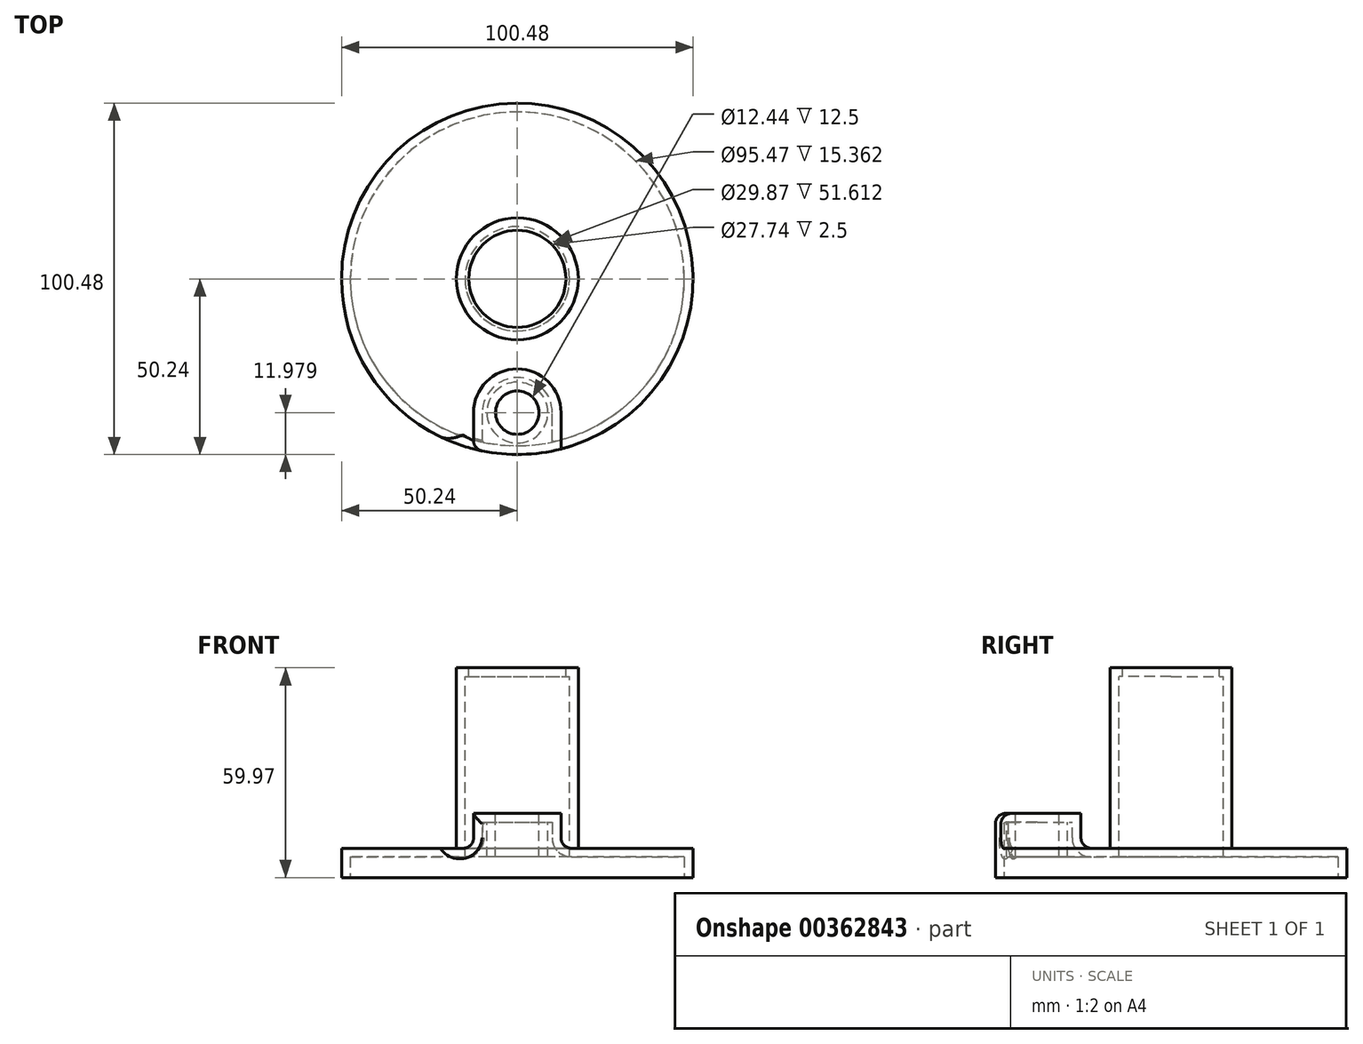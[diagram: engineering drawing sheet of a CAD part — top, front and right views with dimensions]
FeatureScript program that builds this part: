
annotation { "Feature Type Name" : "Feature", "Feature Type Description" : "" }
export const myFeature = defineFeature(function(context is Context, id is Id, definition is map)
    precondition{}
    {
        {
            var Q0;
            Q0=qCreatedBy(makeId("Right.planeOp"),FACE);
            var sketch = newSketch(context, id + "F0", { "sketchPlane" : qUnion([Q0])});
            skLineSegment(sketch, "E0.bottom", {"start": v(0, 0) * mm, "end": v(-50.24, 0) * mm});
            skLineSegment(sketch, "E0.top", {"start": v(0, 59.97) * mm, "end": v(-50.24, 59.97) * mm});
            skLineSegment(sketch, "E0.left", {"start": v(0, 0) * mm, "end": v(0, 59.97) * mm});
            skLineSegment(sketch, "E0.right", {"start": v(-50.24, 0) * mm, "end": v(-50.24, 59.97) * mm});
            skLineSegment(sketch, "E1", {"start": v(0, -25.53) * mm, "end": v(0, 77.83) * mm, "construction": true});
            skSolve(sketch);
        }
        {
            var Q0;
            Q0 = qSketchRegion(id + "F0", true);
            var Q1;
            Q1=sQuery(id+"F0.wireOp",EDGE,"E1");
            revolve(context, id + "F1", {"entities" : qUnion([Q0]), "axis" : qUnion([Q1]), "revolveType" : RevolveType.FULL});
        }
        {
            var Q0;
            Q0=qCreatedBy(makeId("Right.planeOp"),FACE);
            var sketch = newSketch(context, id + "F2", { "sketchPlane" : qUnion([Q0])});
            skLineSegment(sketch, "E2.bottom", {"start": v(-70.29, 84.7) * mm, "end": v(-17.44, 84.7) * mm});
            skLineSegment(sketch, "E2.top", {"start": v(-70.29, 18.36) * mm, "end": v(-17.44, 18.36) * mm});
            skLineSegment(sketch, "E2.left", {"start": v(-70.29, 84.7) * mm, "end": v(-70.29, 18.36) * mm});
            skLineSegment(sketch, "E2.right", {"start": v(-17.44, 84.7) * mm, "end": v(-17.44, 18.36) * mm});
            skSolve(sketch);
        }
        {
            var Q0;
            Q0=makeQuery(id+"F2.imprint","IMPRINT",FACE,{"disambiguationData":[TD([[makeQuery(id+"F2.imprint","IMPRINT",EDGE,{"derivedFrom":sQuery(id+"F2.wireOp",EDGE,"E2.bottom")}),-1.0]])]});
            var Q1;
            Q1=sQuery(id+"F0.wireOp",EDGE,"E1");
            revolve(context, id + "F3", {"operationType" : NewBodyOperationType.REMOVE, "entities" : qUnion([Q0]), "axis" : qUnion([Q1]), "revolveType" : RevolveType.FULL, "oppositeDirection" : true});
        }
        {
            var Q0;
            Q0=makeQuery(id+"F3.boolean.opBoolean","COPY",FACE,{"derivedFrom":makeQuery(id+"F3.opRevolve","SWEPT_FACE",FACE,{"disambiguationData":[OSD([sQuery(id+"F2.wireOp",EDGE,"E2.top")])]})});
            var sketch = newSketch(context, id + "F4", { "sketchPlane" : qUnion([Q0])});
            skLineSegment(sketch, "E3", {"start": v(0, -68.26) * mm, "end": v(0, -38.26) * mm});
            skArc(sketch, "E4.0.startCap", {"start": v(12.5, -68.26) * mm, "mid": v(0, -80.76) * mm, "end": v(-12.5, -68.26) * mm});
            skArc(sketch, "E4.0.endCap", {"start": v(-12.5, -38.26) * mm, "mid": v(0, -25.76) * mm, "end": v(12.5, -38.26) * mm});
            skLineSegment(sketch, "E4.0.left", {"start": v(-12.5, -68.26) * mm, "end": v(-12.5, -38.26) * mm});
            skLineSegment(sketch, "E4.0.right", {"start": v(12.5, -68.26) * mm, "end": v(12.5, -38.26) * mm});
            skCircle(sketch, "E5", {"center": v(0, -38.26) * mm, "radius": 6.22 * mm});
            skSolve(sketch);
        }
        {
            var Q0;
            {var subQ1=sQuery(id+"F4.wireOp",EDGE,"E4.0.endCap");Q0=makeQuery(id+"F4.imprint","IMPRINT",FACE,{"disambiguationData":[TD([[makeQuery(id+"F4.imprint","IMPRINT",EDGE,{"derivedFrom":subQ1}),-1.0]])]});}
            var Q1;
            Q1=makeQuery(id+"F4.imprint","IMPRINT",FACE,{"disambiguationData":[TD([[makeQuery(id+"F4.imprint","IMPRINT",EDGE,{"derivedFrom":sQuery(id+"F4.wireOp",EDGE,"E5")}),1.0]])]});
            extrude(context, id + "F5", {"entities" : qUnion([Q0, Q1]), "operationType" : NewBodyOperationType.REMOVE, "oppositeDirection" : true, "depth" : 10 * mm});
        }
        {
            var Q0;
            Q0=makeQuery(id+"Ff13ZRt0uXcgMN7_1.3.F5.boolean.opBoolean","COPY",EDGE,{"derivedFrom":makeQuery(id+"Ff13ZRt0uXcgMN7_1.3.F5.opExtrude","CAP_EDGE",EDGE,{"disambiguationData":[OSD([sQuery(id+"F4.wireOp",EDGE,"E4.0.left")])],"isStart":true})});
            var Q1;
            Q1=makeQuery(id+"Ff13ZRt0uXcgMN7_1.4.F5.boolean.opBoolean","COPY",EDGE,{"derivedFrom":makeQuery(id+"Ff13ZRt0uXcgMN7_1.4.F5.opExtrude","CAP_EDGE",EDGE,{"disambiguationData":[OSD([sQuery(id+"F4.wireOp",EDGE,"E4.0.right")])],"isStart":true})});
            var Q2;
            Q2=makeQuery(id+"Ff13ZRt0uXcgMN7_1.2.F5.boolean.opBoolean","COPY",EDGE,{"derivedFrom":makeQuery(id+"Ff13ZRt0uXcgMN7_1.2.F5.opExtrude","CAP_EDGE",EDGE,{"disambiguationData":[OSD([sQuery(id+"F4.wireOp",EDGE,"E4.0.left")])],"isStart":true})});
            var Q3;
            Q3=makeQuery(id+"Ff13ZRt0uXcgMN7_1.1.F5.boolean.opBoolean","COPY",EDGE,{"derivedFrom":makeQuery(id+"Ff13ZRt0uXcgMN7_1.1.F5.opExtrude","CAP_EDGE",EDGE,{"disambiguationData":[OSD([sQuery(id+"F4.wireOp",EDGE,"E4.0.left")])],"isStart":true})});
            var Q4;
            Q4=makeQuery(id+"F5.boolean.opBoolean","COPY",EDGE,{"derivedFrom":makeQuery(id+"F5.opExtrude","CAP_EDGE",EDGE,{"disambiguationData":[OSD([sQuery(id+"F4.wireOp",EDGE,"E4.0.left")])],"isStart":true})});
            var Q5;
            Q5=makeQuery(id+"Ff13ZRt0uXcgMN7_1.1.F5.boolean.opBoolean","COPY",EDGE,{"derivedFrom":makeQuery(id+"Ff13ZRt0uXcgMN7_1.1.F5.opExtrude","CAP_EDGE",EDGE,{"disambiguationData":[OSD([sQuery(id+"F4.wireOp",EDGE,"E4.0.endCap")])],"isStart":false})});
            var Q6;
            Q6=makeQuery(id+"Ff13ZRt0uXcgMN7_1.2.F5.boolean.opBoolean","COPY",EDGE,{"derivedFrom":makeQuery(id+"Ff13ZRt0uXcgMN7_1.2.F5.opExtrude","CAP_EDGE",EDGE,{"disambiguationData":[OSD([sQuery(id+"F4.wireOp",EDGE,"E4.0.endCap")])],"isStart":false})});
            var Q7;
            Q7=makeQuery(id+"Ff13ZRt0uXcgMN7_1.3.F5.boolean.opBoolean","COPY",EDGE,{"derivedFrom":makeQuery(id+"Ff13ZRt0uXcgMN7_1.3.F5.opExtrude","CAP_EDGE",EDGE,{"disambiguationData":[OSD([sQuery(id+"F4.wireOp",EDGE,"E4.0.left")])],"isStart":false})});
            var Q8;
            Q8=makeQuery(id+"Ff13ZRt0uXcgMN7_1.4.F5.boolean.opBoolean","COPY",EDGE,{"derivedFrom":makeQuery(id+"Ff13ZRt0uXcgMN7_1.4.F5.opExtrude","CAP_EDGE",EDGE,{"disambiguationData":[OSD([sQuery(id+"F4.wireOp",EDGE,"E4.0.right")])],"isStart":false})});
            var Q9;
            Q9=makeQuery(id+"F5.boolean.opBoolean","COPY",EDGE,{"derivedFrom":makeQuery(id+"F5.opExtrude","CAP_EDGE",EDGE,{"disambiguationData":[OSD([sQuery(id+"F4.wireOp",EDGE,"E4.0.right")])],"isStart":false})});
            var Q10;
            {var subQ0=makeQuery(id+"F1.opRevolve","SWEPT_FACE",FACE,{"disambiguationData":[OSD([sQuery(id+"F0.wireOp",EDGE,"E0.right")])]});var subQ1=makeQuery(id+"Ff13ZRt0uXcgMN7_1.1.F5.opExtrude","SWEPT_FACE",FACE,{"disambiguationData":[OSD([sQuery(id+"F4.wireOp",EDGE,"E4.0.left")])]});var subQ2=makeQuery(id+"F3.opRevolve","SWEPT_FACE",FACE,{"disambiguationData":[OSD([sQuery(id+"F2.wireOp",EDGE,"E2.top")])]});var subQ4=sQuery(id+"F4.wireOp",EDGE,"E4.0.right");Q10=makeQuery(id+"Ff13ZRt0uXcgMN7_1.2.F5.boolean.opBoolean","SPLIT",EDGE,{"disambiguationData":[TD([makeQuery(id+"Ff13ZRt0uXcgMN7_1.1.F5.boolean.opBoolean","COPY",FACE,{"derivedFrom":subQ1})])],"derivedFrom":makeQuery(id+"Ff13ZRt0uXcgMN7_1.1.F5.boolean.opBoolean","SPLIT",EDGE,{"disambiguationData":[TD([makeQuery(id+"F5.boolean.opBoolean","COPY",FACE,{"derivedFrom":makeQuery(id+"F5.opExtrude","SWEPT_FACE",FACE,{"disambiguationData":[OSD([subQ4])]})})])],"derivedFrom":makeQuery(id+"F3.boolean.opBoolean","INTERSECT",EDGE,{"derivedFrom":[subQ0,subQ2]})})});}
            var Q11;
            {var subQ0=makeQuery(id+"F1.opRevolve","SWEPT_FACE",FACE,{"disambiguationData":[OSD([sQuery(id+"F0.wireOp",EDGE,"E0.right")])]});var subQ1=makeQuery(id+"F3.opRevolve","SWEPT_FACE",FACE,{"disambiguationData":[OSD([sQuery(id+"F2.wireOp",EDGE,"E2.top")])]});Q11=makeQuery(id+"Ff13ZRt0uXcgMN7_1.1.F5.boolean.opBoolean","SPLIT",EDGE,{"disambiguationData":[TD([makeQuery(id+"F5.boolean.opBoolean","COPY",FACE,{"derivedFrom":makeQuery(id+"F5.opExtrude","SWEPT_FACE",FACE,{"disambiguationData":[OSD([sQuery(id+"F4.wireOp",EDGE,"E4.0.left")])]})})])],"derivedFrom":makeQuery(id+"F3.boolean.opBoolean","INTERSECT",EDGE,{"derivedFrom":[subQ0,subQ1]})});}
            var Q12;
            {var subQ0=makeQuery(id+"F1.opRevolve","SWEPT_FACE",FACE,{"disambiguationData":[OSD([sQuery(id+"F0.wireOp",EDGE,"E0.right")])]});var subQ1=makeQuery(id+"F3.opRevolve","SWEPT_FACE",FACE,{"disambiguationData":[OSD([sQuery(id+"F2.wireOp",EDGE,"E2.top")])]});var subQ4=makeQuery(id+"F5.boolean.opBoolean","COPY",FACE,{"derivedFrom":makeQuery(id+"F5.opExtrude","SWEPT_FACE",FACE,{"disambiguationData":[OSD([sQuery(id+"F4.wireOp",EDGE,"E4.0.right")])]})});Q12=makeQuery(id+"Ff13ZRt0uXcgMN7_1.4.F5.boolean.opBoolean","SPLIT",EDGE,{"disambiguationData":[TD([subQ4])],"derivedFrom":makeQuery(id+"Ff13ZRt0uXcgMN7_1.3.F5.boolean.opBoolean","SPLIT",EDGE,{"disambiguationData":[TD([subQ4])],"derivedFrom":makeQuery(id+"Ff13ZRt0uXcgMN7_1.2.F5.boolean.opBoolean","SPLIT",EDGE,{"disambiguationData":[TD([subQ4])],"derivedFrom":makeQuery(id+"Ff13ZRt0uXcgMN7_1.1.F5.boolean.opBoolean","SPLIT",EDGE,{"disambiguationData":[TD([subQ4])],"derivedFrom":makeQuery(id+"F3.boolean.opBoolean","INTERSECT",EDGE,{"derivedFrom":[subQ0,subQ1]})})})})});}
            var Q13;
            {var subQ0=makeQuery(id+"F1.opRevolve","SWEPT_FACE",FACE,{"disambiguationData":[OSD([sQuery(id+"F0.wireOp",EDGE,"E0.right")])]});var subQ1=makeQuery(id+"F3.opRevolve","SWEPT_FACE",FACE,{"disambiguationData":[OSD([sQuery(id+"F2.wireOp",EDGE,"E2.top")])]});var subQ3=sQuery(id+"F4.wireOp",EDGE,"E4.0.left");var subQ4=makeQuery(id+"Ff13ZRt0uXcgMN7_1.3.F5.opExtrude","SWEPT_FACE",FACE,{"disambiguationData":[OSD([subQ3])]});var subQ5=sQuery(id+"F4.wireOp",EDGE,"E4.0.right");var subQ6=makeQuery(id+"F5.boolean.opBoolean","COPY",FACE,{"derivedFrom":makeQuery(id+"F5.opExtrude","SWEPT_FACE",FACE,{"disambiguationData":[OSD([subQ5])]})});Q13=makeQuery(id+"Ff13ZRt0uXcgMN7_1.4.F5.boolean.opBoolean","SPLIT",EDGE,{"disambiguationData":[TD([makeQuery(id+"Ff13ZRt0uXcgMN7_1.3.F5.boolean.opBoolean","COPY",FACE,{"derivedFrom":subQ4})])],"derivedFrom":makeQuery(id+"Ff13ZRt0uXcgMN7_1.3.F5.boolean.opBoolean","SPLIT",EDGE,{"disambiguationData":[TD([subQ6])],"derivedFrom":makeQuery(id+"Ff13ZRt0uXcgMN7_1.2.F5.boolean.opBoolean","SPLIT",EDGE,{"disambiguationData":[TD([subQ6])],"derivedFrom":makeQuery(id+"Ff13ZRt0uXcgMN7_1.1.F5.boolean.opBoolean","SPLIT",EDGE,{"disambiguationData":[TD([subQ6])],"derivedFrom":makeQuery(id+"F3.boolean.opBoolean","INTERSECT",EDGE,{"derivedFrom":[subQ0,subQ1]})})})})});}
            var Q14;
            {var subQ0=makeQuery(id+"F1.opRevolve","SWEPT_FACE",FACE,{"disambiguationData":[OSD([sQuery(id+"F0.wireOp",EDGE,"E0.right")])]});var subQ1=makeQuery(id+"F3.opRevolve","SWEPT_FACE",FACE,{"disambiguationData":[OSD([sQuery(id+"F2.wireOp",EDGE,"E2.top")])]});var subQ3=sQuery(id+"F4.wireOp",EDGE,"E4.0.left");var subQ4=makeQuery(id+"Ff13ZRt0uXcgMN7_1.2.F5.opExtrude","SWEPT_FACE",FACE,{"disambiguationData":[OSD([subQ3])]});var subQ5=sQuery(id+"F4.wireOp",EDGE,"E4.0.right");var subQ6=makeQuery(id+"F5.boolean.opBoolean","COPY",FACE,{"derivedFrom":makeQuery(id+"F5.opExtrude","SWEPT_FACE",FACE,{"disambiguationData":[OSD([subQ5])]})});Q14=makeQuery(id+"Ff13ZRt0uXcgMN7_1.3.F5.boolean.opBoolean","SPLIT",EDGE,{"disambiguationData":[TD([makeQuery(id+"Ff13ZRt0uXcgMN7_1.2.F5.boolean.opBoolean","COPY",FACE,{"derivedFrom":subQ4})])],"derivedFrom":makeQuery(id+"Ff13ZRt0uXcgMN7_1.2.F5.boolean.opBoolean","SPLIT",EDGE,{"disambiguationData":[TD([subQ6])],"derivedFrom":makeQuery(id+"Ff13ZRt0uXcgMN7_1.1.F5.boolean.opBoolean","SPLIT",EDGE,{"disambiguationData":[TD([subQ6])],"derivedFrom":makeQuery(id+"F3.boolean.opBoolean","INTERSECT",EDGE,{"derivedFrom":[subQ0,subQ1]})})})});}
            var Q15;
            Q15=makeQuery(id+"Ff13ZRt0uXcgMN7_1.1.F5.boolean.opBoolean","INTERSECT",EDGE,{"derivedFrom":[makeQuery(id+"F1.opRevolve","SWEPT_FACE",FACE,{"disambiguationData":[OSD([sQuery(id+"F0.wireOp",EDGE,"E0.right")])]}),makeQuery(id+"Ff13ZRt0uXcgMN7_1.1.F5.opExtrude","SWEPT_FACE",FACE,{"disambiguationData":[OSD([sQuery(id+"F4.wireOp",EDGE,"E4.0.right")])]})]});
            var Q16;
            Q16=makeQuery(id+"F5.boolean.opBoolean","INTERSECT",EDGE,{"derivedFrom":[makeQuery(id+"F1.opRevolve","SWEPT_FACE",FACE,{"disambiguationData":[OSD([sQuery(id+"F0.wireOp",EDGE,"E0.right")])]}),makeQuery(id+"F5.opExtrude","SWEPT_FACE",FACE,{"disambiguationData":[OSD([sQuery(id+"F4.wireOp",EDGE,"E4.0.left")])]})]});
            var Q17;
            Q17=makeQuery(id+"Ff13ZRt0uXcgMN7_1.4.F5.boolean.opBoolean","INTERSECT",EDGE,{"derivedFrom":[makeQuery(id+"F1.opRevolve","SWEPT_FACE",FACE,{"disambiguationData":[OSD([sQuery(id+"F0.wireOp",EDGE,"E0.right")])]}),makeQuery(id+"Ff13ZRt0uXcgMN7_1.4.F5.opExtrude","SWEPT_FACE",FACE,{"disambiguationData":[OSD([sQuery(id+"F4.wireOp",EDGE,"E4.0.right")])]})]});
            var Q18;
            Q18=makeQuery(id+"Ff13ZRt0uXcgMN7_1.2.F5.boolean.opBoolean","INTERSECT",EDGE,{"derivedFrom":[makeQuery(id+"F1.opRevolve","SWEPT_FACE",FACE,{"disambiguationData":[OSD([sQuery(id+"F0.wireOp",EDGE,"E0.right")])]}),makeQuery(id+"Ff13ZRt0uXcgMN7_1.2.F5.opExtrude","SWEPT_FACE",FACE,{"disambiguationData":[OSD([sQuery(id+"F4.wireOp",EDGE,"E4.0.left")])]})]});
            var Q19;
            Q19=makeQuery(id+"Ff13ZRt0uXcgMN7_1.3.F5.boolean.opBoolean","INTERSECT",EDGE,{"derivedFrom":[makeQuery(id+"F1.opRevolve","SWEPT_FACE",FACE,{"disambiguationData":[OSD([sQuery(id+"F0.wireOp",EDGE,"E0.right")])]}),makeQuery(id+"Ff13ZRt0uXcgMN7_1.3.F5.opExtrude","SWEPT_FACE",FACE,{"disambiguationData":[OSD([sQuery(id+"F4.wireOp",EDGE,"E4.0.left")])]})]});
            var Q20;
            Q20=makeQuery(id+"F3.boolean.opBoolean","COPY",EDGE,{"derivedFrom":makeQuery(id+"F3.opRevolve","SWEPT_EDGE",EDGE,{"disambiguationData":[OSD([sQuery(id+"F2.wireOp",EDGE,"E2.top"),sQuery(id+"F2.wireOp",EDGE,"E2.right")])]})});
            var Q21;
            Q21=makeQuery(id+"Ff13ZRt0uXcgMN7_1.4.F5.boolean.opBoolean","COPY",EDGE,{"derivedFrom":makeQuery(id+"Ff13ZRt0uXcgMN7_1.4.F5.opExtrude","SWEPT_EDGE",EDGE,{"disambiguationData":[OSD([sQuery(id+"F0.wireOp",EDGE,"E0.right"),sQuery(id+"F2.wireOp",EDGE,"E2.top"),sQuery(id+"F4.wireOp",EDGE,"E4.0.left")])]})});
            var Q22;
            Q22=makeQuery(id+"Ff13ZRt0uXcgMN7_1.3.F5.boolean.opBoolean","COPY",EDGE,{"derivedFrom":makeQuery(id+"Ff13ZRt0uXcgMN7_1.3.F5.opExtrude","SWEPT_EDGE",EDGE,{"disambiguationData":[OSD([sQuery(id+"F0.wireOp",EDGE,"E0.right"),sQuery(id+"F2.wireOp",EDGE,"E2.top"),sQuery(id+"F4.wireOp",EDGE,"E4.0.left")])]})});
            var Q23;
            Q23=makeQuery(id+"F5.boolean.opBoolean","COPY",EDGE,{"derivedFrom":makeQuery(id+"F5.opExtrude","SWEPT_EDGE",EDGE,{"disambiguationData":[OSD([sQuery(id+"F0.wireOp",EDGE,"E0.right"),sQuery(id+"F2.wireOp",EDGE,"E2.top"),sQuery(id+"F4.wireOp",EDGE,"E4.0.left")])]})});
            var Q24;
            Q24=makeQuery(id+"Ff13ZRt0uXcgMN7_1.1.F5.boolean.opBoolean","COPY",EDGE,{"derivedFrom":makeQuery(id+"Ff13ZRt0uXcgMN7_1.1.F5.opExtrude","SWEPT_EDGE",EDGE,{"disambiguationData":[OSD([sQuery(id+"F0.wireOp",EDGE,"E0.right"),sQuery(id+"F2.wireOp",EDGE,"E2.top"),sQuery(id+"F4.wireOp",EDGE,"E4.0.left")])]})});
            var Q25;
            Q25=makeQuery(id+"Ff13ZRt0uXcgMN7_1.2.F5.boolean.opBoolean","COPY",EDGE,{"derivedFrom":makeQuery(id+"Ff13ZRt0uXcgMN7_1.2.F5.opExtrude","SWEPT_EDGE",EDGE,{"disambiguationData":[OSD([sQuery(id+"F0.wireOp",EDGE,"E0.right"),sQuery(id+"F2.wireOp",EDGE,"E2.top"),sQuery(id+"F4.wireOp",EDGE,"E4.0.left")])]})});
            fillet(context, id + "F6", {"entities" : qUnion([Q0, Q1, Q2, Q3, Q4, Q5, Q6, Q7, Q8, Q9, Q10, Q11, Q12, Q13, Q14, Q15, Q16, Q17, Q18, Q19, Q20, Q21, Q22, Q23, Q24, Q25]), "radius" : 3 * mm, "tangentPropagation" : true, "allowEdgeOverflow" : false});
        }
        {
            var Q0;
            Q0=makeQuery(id+"F1.opRevolve","SWEPT_FACE",FACE,{"disambiguationData":[OSD([sQuery(id+"F0.wireOp",EDGE,"E0.bottom")])]});
            shell(context, id + "F7", {"entities" : qUnion([Q0]), "thickness" : 2.5 * mm});
        }
        {
            var Q0;
            Q0=makeQuery(id+"F1.opRevolve","SWEPT_FACE",FACE,{"disambiguationData":[OSD([sQuery(id+"F0.wireOp",EDGE,"E0.top")])]});
            var sketch = newSketch(context, id + "F8", { "sketchPlane" : qUnion([Q0])});
            skCircle(sketch, "E6", {"center": v(0, 0) * mm, "radius": 13.87 * mm});
            skSolve(sketch);
        }
        {
            var Q0;
            Q0 = qSketchRegion(id + "F8", true);
            extrude(context, id + "F9", {"entities" : qUnion([Q0]), "operationType" : NewBodyOperationType.REMOVE, "oppositeDirection" : true, "depth" : 25 * mm});
        }
        {
            var Q0;
            Q0=makeQuery(id+"F4.imprint","IMPRINT",FACE,{"disambiguationData":[TD([[makeQuery(id+"F4.imprint","IMPRINT",EDGE,{"derivedFrom":sQuery(id+"F4.wireOp",EDGE,"E5")}),1.0]])]});
            extrude(context, id + "F10", {"entities" : qUnion([Q0]), "operationType" : NewBodyOperationType.REMOVE, "endBound" : BoundingType.THROUGH_ALL, "oppositeDirection" : true, "depth" : 25 * mm});
        }
    });
